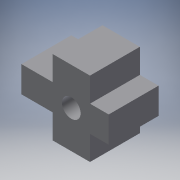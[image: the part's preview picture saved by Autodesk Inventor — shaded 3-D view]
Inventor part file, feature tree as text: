
AUTODESK INVENTOR PART (.ipt)
format: ipt  version: 2016 (Build 200138000, 138)  size: 103,936 bytes
history: native  units: mm
features: other x3, extrude x1, hole x1
ambient origin geometry x8: Origin, YZ Plane, XZ Plane, XY Plane, X Axis, Y Axis, Z Axis, Center Point
bodies: Solid1 (feature_tree)
feature tree (5):
  other  "zero_sketch.ipt"
  extrude  "Extrusion1"  Depth=10.0mm
  hole  "Hole1"  [1 undecoded]
  other  "base+body"
  other  "base+body_1"
note: 1 required parameter value undecoded (feature->parameter linkage not recoverable at this tier; creation-order binding heuristic only, values carry confidence <= 0.55)
